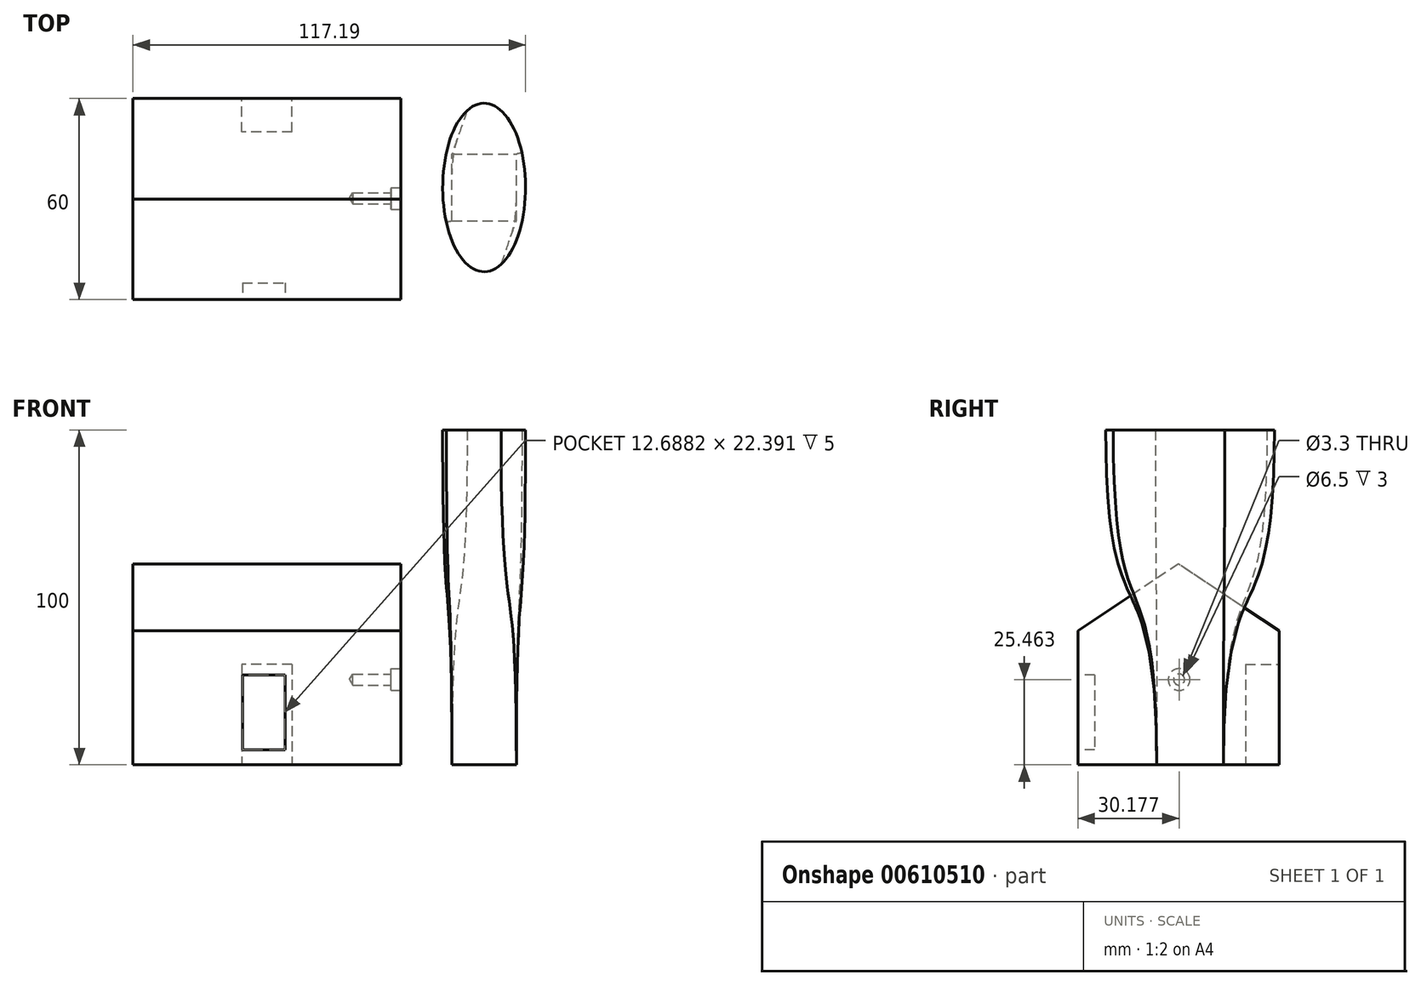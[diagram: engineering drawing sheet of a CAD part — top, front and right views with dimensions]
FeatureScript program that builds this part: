
annotation { "Feature Type Name" : "Feature", "Feature Type Description" : "" }
export const myFeature = defineFeature(function(context is Context, id is Id, definition is map)
    precondition{}
    {
        {
            var Q0;
            Q0=qCreatedBy(makeId("Right.planeOp"),FACE);
            var sketch = newSketch(context, id + "F0", { "sketchPlane" : qUnion([Q0])});
            skLineSegment(sketch, "E0", {"start": v(0, 0) * mm, "end": v(60, 0) * mm});
            skLineSegment(sketch, "E1", {"start": v(60, 0) * mm, "end": v(60, 40) * mm});
            skLineSegment(sketch, "E2", {"start": v(60, 40) * mm, "end": v(30, 60) * mm});
            skLineSegment(sketch, "E3", {"start": v(30, 60) * mm, "end": v(0, 40) * mm});
            skLineSegment(sketch, "E4", {"start": v(0, 40) * mm, "end": v(0, 0) * mm});
            skLineSegment(sketch, "E5", {"start": v(30, 60) * mm, "end": v(30, 0) * mm, "construction": true});
            skSolve(sketch);
        }
        {
            var Q0;
            Q0 = qSketchRegion(id + "F0", true);
            extrude(context, id + "F1", {"entities" : qUnion([Q0]), "depth" : 80 * mm, "offsetDistance" : 25 * mm});
        }
        {
            var Q0;
            Q0=makeQuery(id+"F1.opExtrude","SWEPT_FACE",FACE,{"disambiguationData":[OSD([sQuery(id+"F0.wireOp",EDGE,"E1")])]});
            var sketch = newSketch(context, id + "F2", { "sketchPlane" : qUnion([Q0])});
            skLineSegment(sketch, "E6.bottom", {"start": v(-47.5, 30) * mm, "end": v(-32.5, 30) * mm});
            skLineSegment(sketch, "E6.top", {"start": v(-47.5, 0) * mm, "end": v(-32.5, 0) * mm});
            skLineSegment(sketch, "E6.left", {"start": v(-47.5, 30) * mm, "end": v(-47.5, 0) * mm});
            skLineSegment(sketch, "E6.right", {"start": v(-32.5, 30) * mm, "end": v(-32.5, 0) * mm});
            skLineSegment(sketch, "E7", {"start": v(-40, 40) * mm, "end": v(-40, 30) * mm, "construction": true});
            skSolve(sketch);
        }
        {
            var Q0;
            Q0 = qSketchRegion(id + "F2", true);
            extrude(context, id + "F3", {"entities" : qUnion([Q0]), "operationType" : NewBodyOperationType.REMOVE, "oppositeDirection" : true, "depth" : 10 * mm, "offsetDistance" : 25 * mm});
        }
        {
            var Q0;
            Q0=makeQuery(id+"F1.opExtrude","SWEPT_FACE",FACE,{"disambiguationData":[OSD([sQuery(id+"F0.wireOp",EDGE,"E4")])]});
            var sketch = newSketch(context, id + "F4", { "sketchPlane" : qUnion([Q0])});
            skLineSegment(sketch, "E8.bottom", {"start": v(32.66, 26.84) * mm, "end": v(45.35, 26.84) * mm});
            skLineSegment(sketch, "E8.top", {"start": v(32.66, 4.45) * mm, "end": v(45.35, 4.45) * mm});
            skLineSegment(sketch, "E8.left", {"start": v(32.66, 26.84) * mm, "end": v(32.66, 4.45) * mm});
            skLineSegment(sketch, "E8.right", {"start": v(45.35, 26.84) * mm, "end": v(45.35, 4.45) * mm});
            skSolve(sketch);
        }
        {
            var Q0;
            Q0 = qSketchRegion(id + "F4", true);
            extrude(context, id + "F5", {"entities" : qUnion([Q0]), "operationType" : NewBodyOperationType.REMOVE, "oppositeDirection" : true, "depth" : 5 * mm, "offsetDistance" : 25 * mm});
        }
        {
            var Q0;
            Q0=makeQuery(id+"F1.opExtrude","CAP_FACE",FACE,{"disambiguationData":[OSD([sQuery(id+"F0.wireOp",EDGE,"E0"),sQuery(id+"F0.wireOp",EDGE,"E1"),sQuery(id+"F0.wireOp",EDGE,"E2"),sQuery(id+"F0.wireOp",EDGE,"E3"),sQuery(id+"F0.wireOp",EDGE,"E4")])],"isStart":false});
            var sketch = newSketch(context, id + "F6", { "sketchPlane" : qUnion([Q0])});
            skPoint(sketch, "E9", {"position": v(30.18, 25.46) * mm});
            skSolve(sketch);
        }
        {
            var Q0;
            Q0=sQuery(id+"F6.wireOp",VERTEX,"E9");
            var Q1;
            Q1=makeQuery(id+"F1.opExtrude","SWEPT_BODY",BODY,{"disambiguationData":[OSD([sQuery(id+"F0.wireOp",EDGE,"E0"),sQuery(id+"F0.wireOp",EDGE,"E1"),sQuery(id+"F0.wireOp",EDGE,"E2"),sQuery(id+"F0.wireOp",EDGE,"E3"),sQuery(id+"F0.wireOp",EDGE,"E4")])]});
            hole(context, id + "F7", {"style" : HoleStyle.C_BORE, "endStyle" : HoleEndStyle.BLIND, "standardTappedOrClearance" : lookupTablePath({ "standard" : "ISO", "fit" : "Normal", "size" : "M3", "type" : "Clearance" }), "standardBlindInLast" : lookupTablePath({ "fit" : "Standard", "standard" : "ISO", "size" : "M3", "type" : "Clearance" }), "holeDiameter" : 3.3 * mm, "cBoreDiameter" : 6.5 * mm, "cBoreDepth" : 3 * mm, "majorDiameter" : 5 * mm, "holeDepth" : 14.4 * mm, "isTappedThrough" : true, "tappedDepth" : 12 * mm, "tapClearance" : 3, "locations" : qUnion([Q0]), "scope" : qUnion([Q1])});
        }
        {
            var Q0;
            Q0=makeQuery(id+"F1.opExtrude","CAP_EDGE",EDGE,{"disambiguationData":[OSD([sQuery(id+"F0.wireOp",EDGE,"E1")])],"isStart":false});
            var Q1;
            Q1=makeQuery(id+"F1.opExtrude","CAP_VERTEX",VERTEX,{"disambiguationData":[OSD([sQuery(id+"F0.wireOp",EDGE,"E1"),sQuery(id+"F0.wireOp",EDGE,"E2")])],"isStart":false});
            cPlane(context, id + "F8", {"entities" : qUnion([Q0, Q1]), "cplaneType" : CPlaneType.LINE_POINT, "offset" : 25 * mm, "width" : 150 * mm, "height" : 150 * mm});
        }
        {
            var Q0;
            Q0=qCreatedBy(id+"F8.planeOp",FACE);
            var sketch = newSketch(context, id + "F9", { "sketchPlane" : qUnion([Q0])});
            skLineSegment(sketch, "E10", {"start": v(91.37, 80.14) * mm, "end": v(6.35, 80.14) * mm});
            skLineSegment(sketch, "E11", {"start": v(-8.65, 65.14) * mm, "end": v(-8.65, 8.34) * mm});
            skPoint(sketch, "E12.visualSharp", {"position": v(-8.65, 80.14) * mm});
            skArc(sketch, "E12.filletArc", {"start": v(6.35, 80.14) * mm, "mid": v(-4.26, 75.75) * mm, "end": v(-8.65, 65.14) * mm});
            skSolve(sketch);
        }
        {
            var Q0;
            Q0=sQuery(id+"F9.wireOp",EDGE,"E10");
            var Q1;
            Q1=sQuery(id+"F9.wireOp",VERTEX,"E10.start");
            cPlane(context, id + "F10", {"entities" : qUnion([Q0, Q1]), "cplaneType" : CPlaneType.LINE_POINT, "offset" : 25 * mm, "width" : 150 * mm, "height" : 150 * mm});
        }
        {
            var Q0;
            Q0=makeQuery(id+"F1.opExtrude","SWEPT_FACE",FACE,{"disambiguationData":[OSD([sQuery(id+"F0.wireOp",EDGE,"E0")])]});
            var sketch = newSketch(context, id + "F11", { "sketchPlane" : qUnion([Q0])});
            skLineSegment(sketch, "E13.bottom", {"start": v(95.2, -23.49) * mm, "end": v(114.44, -23.49) * mm});
            skLineSegment(sketch, "E13.top", {"start": v(95.2, -43.4) * mm, "end": v(114.44, -43.4) * mm});
            skLineSegment(sketch, "E13.left", {"start": v(95.2, -23.49) * mm, "end": v(95.2, -43.4) * mm});
            skLineSegment(sketch, "E13.right", {"start": v(114.44, -23.49) * mm, "end": v(114.44, -43.4) * mm});
            skPoint(sketch, "E13.middle", {"position": v(104.82, -33.45) * mm});
            skSolve(sketch);
        }
        {
            var Q0;
            {var subQ3=sQuery(id+"F0.wireOp",EDGE,"E0");Q0=makeQuery(id+"F11.imprint","IMPRINT",FACE,{"disambiguationData":[TD([[makeQuery(id+"F11.imprint","IMPRINT",EDGE,{"derivedFrom":makeQuery(id+"F1.opExtrude","CAP_EDGE",EDGE,{"disambiguationData":[OSD([subQ3])],"isStart":true})}),1.0]])]});}
            cPlane(context, id + "F12", {"entities" : qUnion([Q0]), "cplaneType" : CPlaneType.OFFSET, "offset" : 100 * mm, "oppositeDirection" : true, "width" : 150 * mm, "height" : 150 * mm});
        }
        {
            var Q0;
            Q0=qCreatedBy(id+"F12.planeOp",FACE);
            var sketch = newSketch(context, id + "F13", { "sketchPlane" : qUnion([Q0])});
            skPoint(sketch, "E14.0", {"position": v(104.82, -33.45) * mm});
            skEllipse(sketch, "E15", {"center": v(104.82, -33.45) * mm, "majorRadius": 25.17 * mm, "minorRadius": 12.37 * mm, "majorAxis": v(0, -1)});
            skSolve(sketch);
        }
        {
            var Q0;
            Q0=makeQuery(id+"F13.imprint","IMPRINT",FACE,{"disambiguationData":[TD([[makeQuery(id+"F13.imprint","IMPRINT",EDGE,{"derivedFrom":sQuery(id+"F13.wireOp",EDGE,"E15")}),1.0]])]});
            var Q1;
            Q1=makeQuery(id+"F11.imprint","IMPRINT",FACE,{"disambiguationData":[TD([[makeQuery(id+"F11.imprint","IMPRINT",EDGE,{"derivedFrom":sQuery(id+"F11.wireOp",EDGE,"E13.bottom")}),-1.0]])]});
            loft(context, id + "F14", {"startCondition" : LoftEndDerivativeType.NORMAL_TO_PROFILE, "startMagnitude" : 2, "endCondition" : LoftEndDerivativeType.NORMAL_TO_PROFILE, "endMagnitude" : 2, "sheetProfilesArray" : [{ "sheetProfileEntities" : qUnion([Q0]) }, { "sheetProfileEntities" : qUnion([Q1]) }]});
        }
    });
